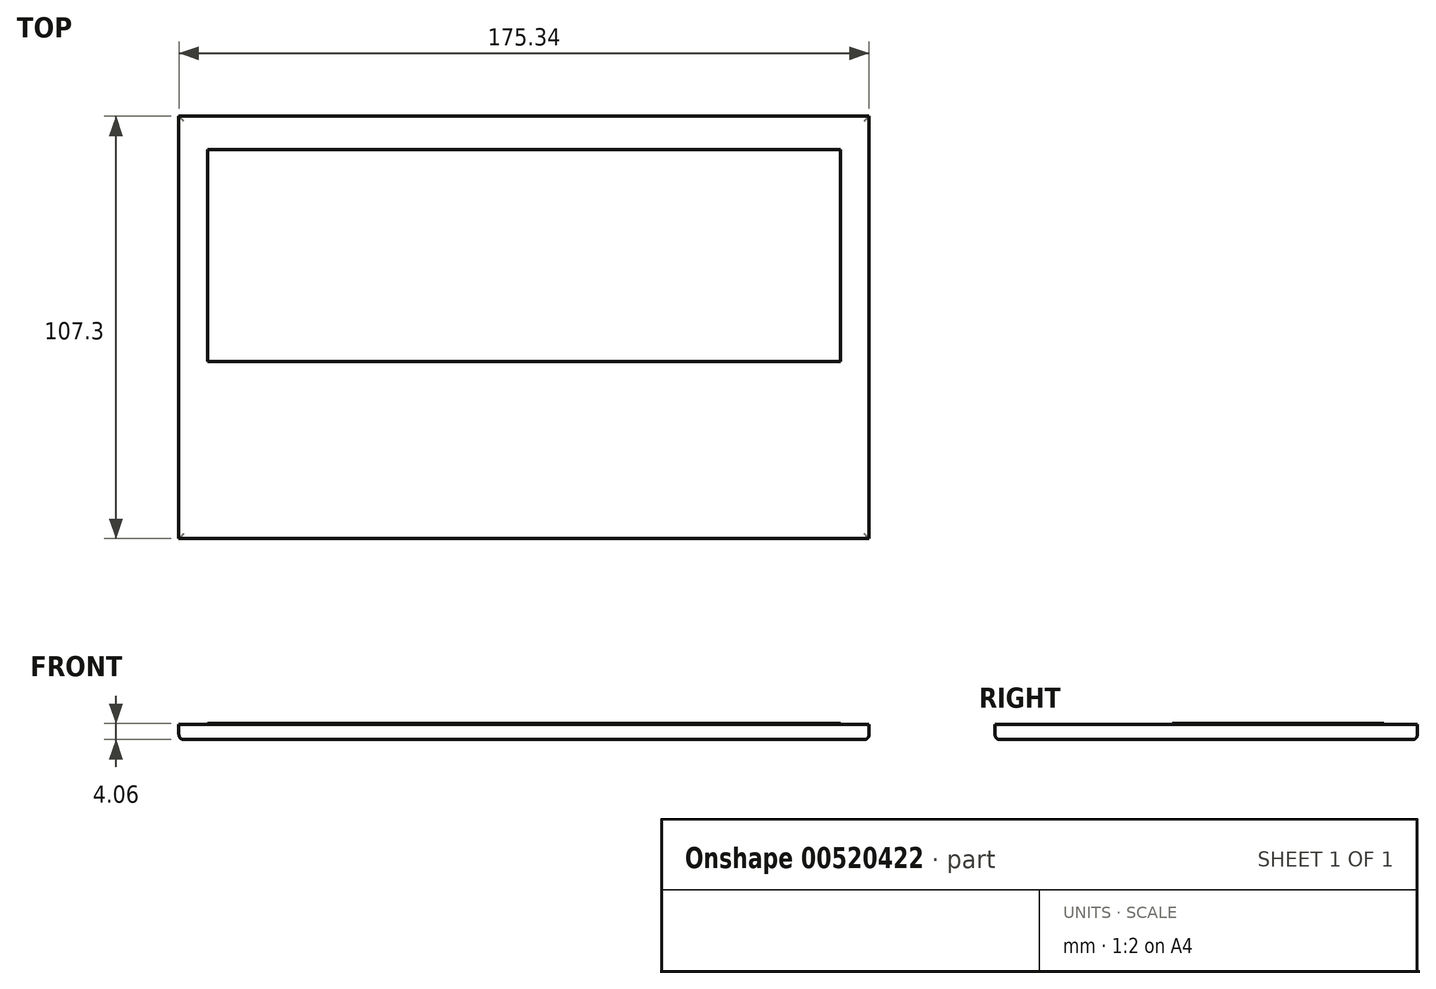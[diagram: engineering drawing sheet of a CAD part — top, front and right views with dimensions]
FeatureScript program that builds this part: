
annotation { "Feature Type Name" : "Feature", "Feature Type Description" : "" }
export const myFeature = defineFeature(function(context is Context, id is Id, definition is map)
    precondition{}
    {
        {
            var Q0;
            Q0=qCreatedBy(makeId("Top.planeOp"),FACE);
            var sketch = newSketch(context, id + "F0", { "sketchPlane" : qUnion([Q0])});
            skLineSegment(sketch, "E0.bottom", {"start": v(87.67, 53.65) * mm, "end": v(-87.67, 53.65) * mm});
            skLineSegment(sketch, "E0.top", {"start": v(87.67, -53.65) * mm, "end": v(-87.67, -53.65) * mm});
            skLineSegment(sketch, "E0.left", {"start": v(87.67, 53.65) * mm, "end": v(87.67, -53.65) * mm});
            skLineSegment(sketch, "E0.right", {"start": v(-87.67, 53.65) * mm, "end": v(-87.67, -53.65) * mm});
            skPoint(sketch, "E0.middle", {"position": v(0, 0) * mm});
            skSolve(sketch);
        }
        {
            var Q0;
            Q0 = qSketchRegion(id + "F0", true);
            extrude(context, id + "F1", {"entities" : qUnion([Q0]), "depth" : 3.8 * mm, "offsetDistance" : 25.4 * mm});
        }
        {
            var Q0;
            Q0=makeQuery(id+"F1.opExtrude","CAP_EDGE",EDGE,{"disambiguationData":[OSD([sQuery(id+"F0.wireOp",EDGE,"E0.left")])],"isStart":true});
            var Q1;
            Q1=makeQuery(id+"F1.opExtrude","CAP_EDGE",EDGE,{"disambiguationData":[OSD([sQuery(id+"F0.wireOp",EDGE,"E0.top")])],"isStart":true});
            var Q2;
            Q2=makeQuery(id+"F1.opExtrude","CAP_EDGE",EDGE,{"disambiguationData":[OSD([sQuery(id+"F0.wireOp",EDGE,"E0.bottom")])],"isStart":true});
            var Q3;
            Q3=makeQuery(id+"F1.opExtrude","CAP_EDGE",EDGE,{"disambiguationData":[OSD([sQuery(id+"F0.wireOp",EDGE,"E0.right")])],"isStart":true});
            fillet(context, id + "F2", {"entities" : qUnion([Q0, Q1, Q2, Q3]), "radius" : 1.27 * mm, "tangentPropagation" : true, "allowEdgeOverflow" : false});
        }
        {
            var Q0;
            Q0=makeQuery(id+"F1.opExtrude","CAP_FACE",FACE,{"disambiguationData":[OSD([sQuery(id+"F0.wireOp",EDGE,"E0.bottom"),sQuery(id+"F0.wireOp",EDGE,"E0.top"),sQuery(id+"F0.wireOp",EDGE,"E0.left"),sQuery(id+"F0.wireOp",EDGE,"E0.right")])],"isStart":false});
            var sketch = newSketch(context, id + "F3", { "sketchPlane" : qUnion([Q0])});
            skLineSegment(sketch, "E1.bottom", {"start": v(36.56, -9.8) * mm, "end": v(-36.56, -9.8) * mm});
            skLineSegment(sketch, "E1.top", {"start": v(36.56, -50.96) * mm, "end": v(-36.56, -50.96) * mm});
            skLineSegment(sketch, "E1.left", {"start": v(36.56, -9.8) * mm, "end": v(36.56, -50.96) * mm});
            skLineSegment(sketch, "E1.right", {"start": v(-36.56, -9.8) * mm, "end": v(-36.56, -50.96) * mm});
            skPoint(sketch, "E1.middle", {"position": v(0, -30.38) * mm});
            skSolve(sketch);
        }
        {
            var Q0;
            Q0 = qSketchRegion(id + "F3", true);
            extrude(context, id + "F4", {"entities" : qUnion([Q0]), "operationType" : NewBodyOperationType.ADD, "oppositeDirection" : true, "depth" : 2.54 * mm, "offsetDistance" : 25.4 * mm});
        }
        {
            var Q0;
            Q0=makeQuery(id+"F1.opExtrude","CAP_FACE",FACE,{"disambiguationData":[OSD([sQuery(id+"F0.wireOp",EDGE,"E0.bottom"),sQuery(id+"F0.wireOp",EDGE,"E0.top"),sQuery(id+"F0.wireOp",EDGE,"E0.left"),sQuery(id+"F0.wireOp",EDGE,"E0.right")])],"isStart":false});
            var sketch = newSketch(context, id + "F5", { "sketchPlane" : qUnion([Q0])});
            skLineSegment(sketch, "E2.bottom", {"start": v(80.37, -8.6) * mm, "end": v(-80.37, -8.6) * mm});
            skLineSegment(sketch, "E2.top", {"start": v(80.37, 45.15) * mm, "end": v(-80.37, 45.15) * mm});
            skLineSegment(sketch, "E2.left", {"start": v(80.37, -8.6) * mm, "end": v(80.37, 45.15) * mm});
            skLineSegment(sketch, "E2.right", {"start": v(-80.37, -8.6) * mm, "end": v(-80.37, 45.15) * mm});
            skPoint(sketch, "E2.middle", {"position": v(0, 18.28) * mm});
            skSolve(sketch);
        }
        {
            var Q0;
            Q0 = qSketchRegion(id + "F5", true);
            extrude(context, id + "F6", {"entities" : qUnion([Q0]), "operationType" : NewBodyOperationType.ADD, "depth" : 0.25 * mm, "offsetDistance" : 25.4 * mm});
        }
    });
